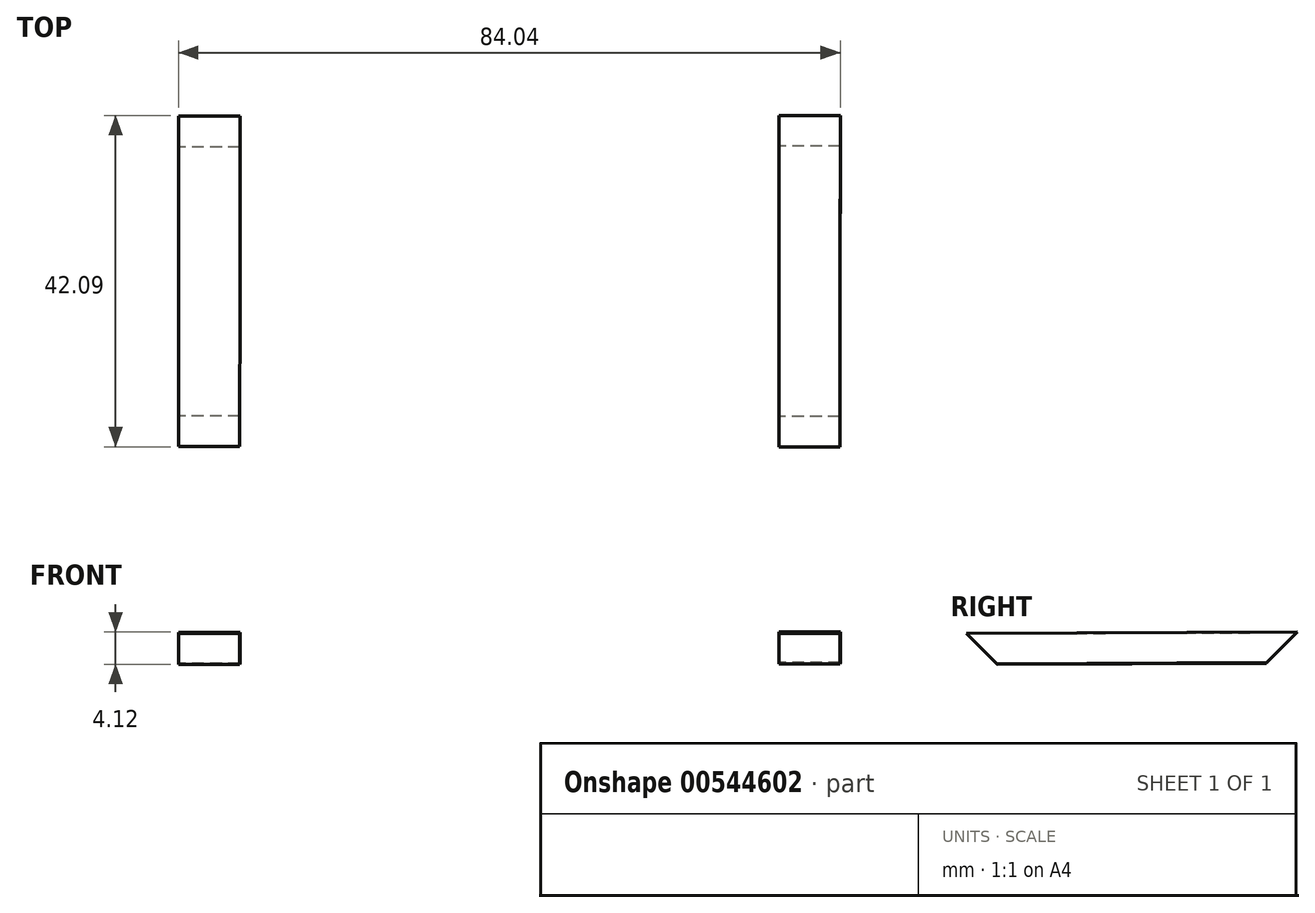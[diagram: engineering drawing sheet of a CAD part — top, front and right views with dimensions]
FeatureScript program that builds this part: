
annotation { "Feature Type Name" : "Feature", "Feature Type Description" : "" }
export const myFeature = defineFeature(function(context is Context, id is Id, definition is map)
    precondition{}
    {
        {
            var Q0;
            Q0=qCreatedBy(makeId("Top.planeOp"),FACE);
            var Q1;
            Q1=qCreatedBy(makeId("Front.planeOp"),FACE);
            cPlane(context, id + "F0", {"entities" : qUnion([Q0, Q1]), "cplaneType" : CPlaneType.MID_PLANE, "offset" : 25.4 * mm, "width" : 152.4 * mm, "height" : 152.4 * mm});
        }
        {
            var Q0;
            Q0=qCreatedBy(makeId("Front.planeOp"),FACE);
            var Q1;
            Q1=qCreatedBy(makeId("Top.planeOp"),FACE);
            cPlane(context, id + "F1", {"entities" : qUnion([Q0, Q1]), "cplaneType" : CPlaneType.MID_PLANE, "offset" : 25.4 * mm, "flipAlignment" : true, "width" : 152.4 * mm, "height" : 152.4 * mm});
        }
        {
            var Q0;
            Q0=qCreatedBy(id+"F0.planeOp",FACE);
            var sketch = newSketch(context, id + "F2", { "sketchPlane" : qUnion([Q0])});
            skLineSegment(sketch, "E0.bottom", {"start": v(-41.91, 29.64) * mm, "end": v(-34.13, 29.64) * mm});
            skLineSegment(sketch, "E0.top", {"start": v(-41.91, 24.14) * mm, "end": v(-34.13, 24.14) * mm});
            skLineSegment(sketch, "E0.left", {"start": v(-41.91, 29.64) * mm, "end": v(-41.91, 24.14) * mm});
            skLineSegment(sketch, "E0.right", {"start": v(-34.13, 29.64) * mm, "end": v(-34.13, 24.14) * mm});
            skPoint(sketch, "E0.middle", {"position": v(-38.02, 26.89) * mm});
            skSolve(sketch);
        }
        {
            var Q0;
            Q0=qCreatedBy(id+"F1.planeOp",FACE);
            var sketch = newSketch(context, id + "F3", { "sketchPlane" : qUnion([Q0])});
            skLineSegment(sketch, "E1.bottom", {"start": v(41.94, 24.37) * mm, "end": v(34.17, 24.37) * mm});
            skLineSegment(sketch, "E1.top", {"start": v(41.94, 29.88) * mm, "end": v(34.17, 29.88) * mm});
            skLineSegment(sketch, "E1.left", {"start": v(41.94, 24.37) * mm, "end": v(41.94, 29.88) * mm});
            skLineSegment(sketch, "E1.right", {"start": v(34.17, 24.37) * mm, "end": v(34.17, 29.88) * mm});
            skPoint(sketch, "E1.middle", {"position": v(38.06, 27.13) * mm});
            skSolve(sketch);
        }
        {
            var Q0;
            Q0=qCreatedBy(id+"F0.planeOp",FACE);
            var sketch = newSketch(context, id + "F4", { "sketchPlane" : qUnion([Q0])});
            skLineSegment(sketch, "E2.bottom", {"start": v(34.33, 29.57) * mm, "end": v(42.1, 29.57) * mm});
            skLineSegment(sketch, "E2.top", {"start": v(34.33, 24.05) * mm, "end": v(42.1, 24.05) * mm});
            skLineSegment(sketch, "E2.left", {"start": v(34.33, 29.57) * mm, "end": v(34.33, 24.05) * mm});
            skLineSegment(sketch, "E2.right", {"start": v(42.1, 29.57) * mm, "end": v(42.1, 24.05) * mm});
            skPoint(sketch, "E2.middle", {"position": v(38.21, 26.81) * mm});
            skSolve(sketch);
        }
        {
            var Q0;
            Q0=qCreatedBy(id+"F1.planeOp",FACE);
            var sketch = newSketch(context, id + "F5", { "sketchPlane" : qUnion([Q0])});
            skLineSegment(sketch, "E3.bottom", {"start": v(-34.3, 24.25) * mm, "end": v(-42.08, 24.25) * mm});
            skLineSegment(sketch, "E3.top", {"start": v(-34.3, 29.76) * mm, "end": v(-42.08, 29.76) * mm});
            skLineSegment(sketch, "E3.left", {"start": v(-34.3, 24.25) * mm, "end": v(-34.3, 29.76) * mm});
            skLineSegment(sketch, "E3.right", {"start": v(-42.08, 24.25) * mm, "end": v(-42.08, 29.76) * mm});
            skPoint(sketch, "E3.middle", {"position": v(-38.19, 27) * mm});
            skSolve(sketch);
        }
        {
            var Q0;
            Q0 = qSketchRegion(id + "F2", true);
            var Q1;
            Q1 = qSketchRegion(id + "F3", true);
            loft(context, id + "F6", {"sheetProfilesArray" : [{ "sheetProfileEntities" : qUnion([Q0]) }, { "sheetProfileEntities" : qUnion([Q1]) }]});
        }
        {
            var Q0;
            Q0 = qSketchRegion(id + "F4", true);
            var Q1;
            Q1 = qSketchRegion(id + "F5", true);
            loft(context, id + "F7", {"sheetProfilesArray" : [{ "sheetProfileEntities" : qUnion([Q0]) }, { "sheetProfileEntities" : qUnion([Q1]) }]});
        }
    });
